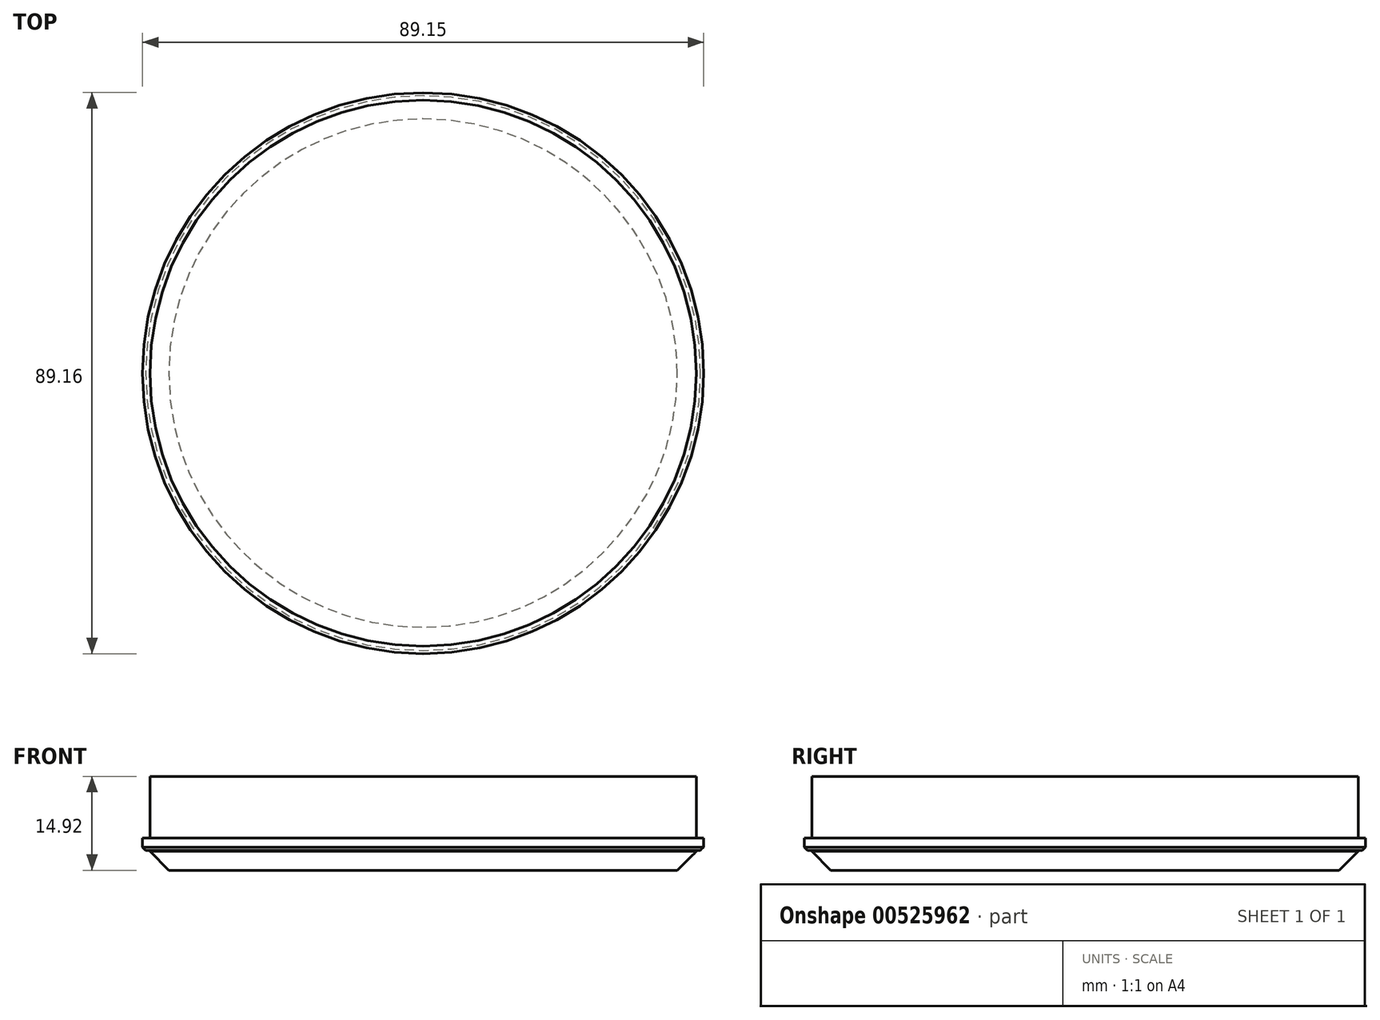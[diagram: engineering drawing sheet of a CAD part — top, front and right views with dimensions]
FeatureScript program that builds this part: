
annotation { "Feature Type Name" : "Feature", "Feature Type Description" : "" }
export const myFeature = defineFeature(function(context is Context, id is Id, definition is map)
    precondition{}
    {
        {
            var Q0;
            Q0=qCreatedBy(makeId("Front.planeOp"),FACE);
            var sketch = newSketch(context, id + "F0", { "sketchPlane" : qUnion([Q0])});
            skLineSegment(sketch, "E0", {"start": v(37.59, -5.54) * mm, "end": v(11.96, -5.54) * mm});
            skLineSegment(sketch, "E1", {"start": v(11.96, -5.54) * mm, "end": v(11.96, 5.6) * mm});
            skLineSegment(sketch, "E2", {"start": v(11.96, 5.6) * mm, "end": v(37.59, 5.6) * mm});
            skLineSegment(sketch, "E3", {"start": v(37.59, 5.6) * mm, "end": v(37.59, -5.54) * mm});
            skLineSegment(sketch, "E4", {"start": v(-6.02, -5.54) * mm, "end": v(-30.31, -5.54) * mm});
            skLineSegment(sketch, "E5", {"start": v(-30.31, -5.54) * mm, "end": v(-30.31, 5.6) * mm});
            skLineSegment(sketch, "E6", {"start": v(-30.31, 5.6) * mm, "end": v(-6.02, 5.6) * mm});
            skLineSegment(sketch, "E7", {"start": v(-6.02, 5.6) * mm, "end": v(-6.02, 1.37) * mm});
            skLineSegment(sketch, "E8", {"start": v(-6.02, 1.37) * mm, "end": v(-7.2, 1.37) * mm});
            skLineSegment(sketch, "E9", {"start": v(-7.2, 1.37) * mm, "end": v(-7.2, -1.5) * mm});
            skLineSegment(sketch, "E10", {"start": v(-7.2, -1.5) * mm, "end": v(-6.02, -1.5) * mm});
            skLineSegment(sketch, "E11", {"start": v(-6.02, -1.5) * mm, "end": v(-6.02, -5.54) * mm});
            skSolve(sketch);
        }
        {
            var Q0;
            Q0=makeQuery(id+"F0.imprint","IMPRINT",FACE,{"disambiguationData":[TD([[makeQuery(id+"F0.imprint","IMPRINT",EDGE,{"derivedFrom":sQuery(id+"F0.wireOp",EDGE,"E4")}),-1.0]])]});
            var sketch = newSketch(context, id + "F1", { "sketchPlane" : qUnion([Q0])});
            skLineSegment(sketch, "E12", {"start": v(-5.63, 10.86) * mm, "end": v(-5.63, 1.04) * mm});
            skLineSegment(sketch, "E13", {"start": v(-5.63, 1.04) * mm, "end": v(-6.81, 1.04) * mm});
            skLineSegment(sketch, "E14", {"start": v(-6.81, 1.04) * mm, "end": v(-6.81, -0.88) * mm});
            skLineSegment(sketch, "E15", {"start": v(-6.81, -0.88) * mm, "end": v(-5.63, -0.88) * mm});
            skLineSegment(sketch, "E16", {"start": v(-5.63, -0.88) * mm, "end": v(-5.63, -4.06) * mm});
            skLineSegment(sketch, "E17", {"start": v(37.77, -4.06) * mm, "end": v(37.77, 10.86) * mm});
            skLineSegment(sketch, "E18", {"start": v(37.77, 10.86) * mm, "end": v(-5.63, 10.86) * mm});
            skLineSegment(sketch, "E19", {"start": v(-5.63, -4.06) * mm, "end": v(37.77, -4.06) * mm});
            skPoint(sketch, "E20.start.orphan", {"position": v(-5.63, -7.24) * mm});
            skSolve(sketch);
        }
        {
            var Q0;
            Q0=makeQuery(id+"F1.imprint","IMPRINT",FACE,{"disambiguationData":[TD([[makeQuery(id+"F1.imprint","IMPRINT",EDGE,{"derivedFrom":sQuery(id+"F1.wireOp",EDGE,"E12")}),1.0]])]});
            var Q1;
            Q1=sQuery(id+"F1.wireOp",EDGE,"E17");
            revolve(context, id + "F2", {"entities" : qUnion([Q0]), "axis" : qUnion([Q1]), "revolveType" : RevolveType.FULL});
        }
        {
            var Q0;
            Q0=makeQuery(id+"F2.opRevolve","SWEPT_EDGE",EDGE,{"disambiguationData":[OSD([sQuery(id+"F1.wireOp",EDGE,"E14"),sQuery(id+"F1.wireOp",EDGE,"E15")])]});
            chamfer(context, id + "F3", {"entities" : qUnion([Q0]), "width" : 0.5 * mm, "tangentPropagation" : true});
        }
        {
            var Q0;
            Q0=makeQuery(id+"F2.opRevolve","SWEPT_EDGE",EDGE,{"disambiguationData":[OSD([sQuery(id+"F1.wireOp",EDGE,"E16"),sQuery(id+"F1.wireOp",EDGE,"E19")])]});
            chamfer(context, id + "F4", {"entities" : qUnion([Q0]), "width" : 3 * mm, "tangentPropagation" : true});
        }
    });
